# Revit family: Temper_88_КранШаровый-ВН_Бабочка
name_source: partatom
category: Арматура трубопроводов
units: mm (PartAtom-declared; Revit-internal decimal feet)

## family parameters
Всегда вертикально = Да
На основе рабочей плоскости = Нет
Общий = Нет
При загрузке вырезать с полостями = Нет
Размер круглого соединителя = Использовать диаметр
Тип детали = Вставляется

## types (4) — shared parameters
ADSK_URL документации изделия = https://brass.temper.ru
ADSK_URL страницы изделия = https://brass.temper.ru
ADSK_Версия Revit = 2019
ADSK_Версия семейства = v1.0
ADSK_Единица измерения = шт.
ADSK_Завод-изготовитель = ООО «ТД «Темпер»
ADSK_Количество = 1
ADSK_Материал = Латунь ЛС59-1В
ADSK_Наименование краткое = Кран шаровой латунный Temper
ADSK_Обозначение = ГОСТ Р 59553-2021
N = 9
Изготовитель = ООО «ТД «Темпер»
Разработчик = https://3dbim.pro
ТВ = ВН
ТВ1 = temper

## per-type parameters (varying)
| type | ADSK_Диаметр условный | ADSK_Код изделия | ADSK_Марка | ADSK_Масса | ADSK_Масса_Текст | ADSK_Наименование |
| DN 15 | 15 мм | 8815ВНБ1240 | 8815ВНБ1240 | 0.15 | 0.15 | Кран шаровой латунный Temper DN15 (12”) PN40 внутренняянаружная бабочка |
| DN 20 | 20 мм | 8820ВНБ3440 | 8820ВНБ3440 | 0.209 | 0.209 | Кран шаровой латунный Temper DN20 (34”) PN40 внутренняянаружная бабочка |
| DN 32 | 32 мм | 8832ВНБ11425 | 8832ВНБ11425 | 0.614 | 0.614 | Кран шаровой латунный Temper DN32 (1 14”) PN25 внутренняянаружная бабочка |
| DN 25 | 25 мм | 8825ВНБ140 | 8825ВНБ140 | 0.332 | 0.332 | Кран шаровой латунный Temper DN25 (1”) PN40 внутренняянаружная бабочка |
